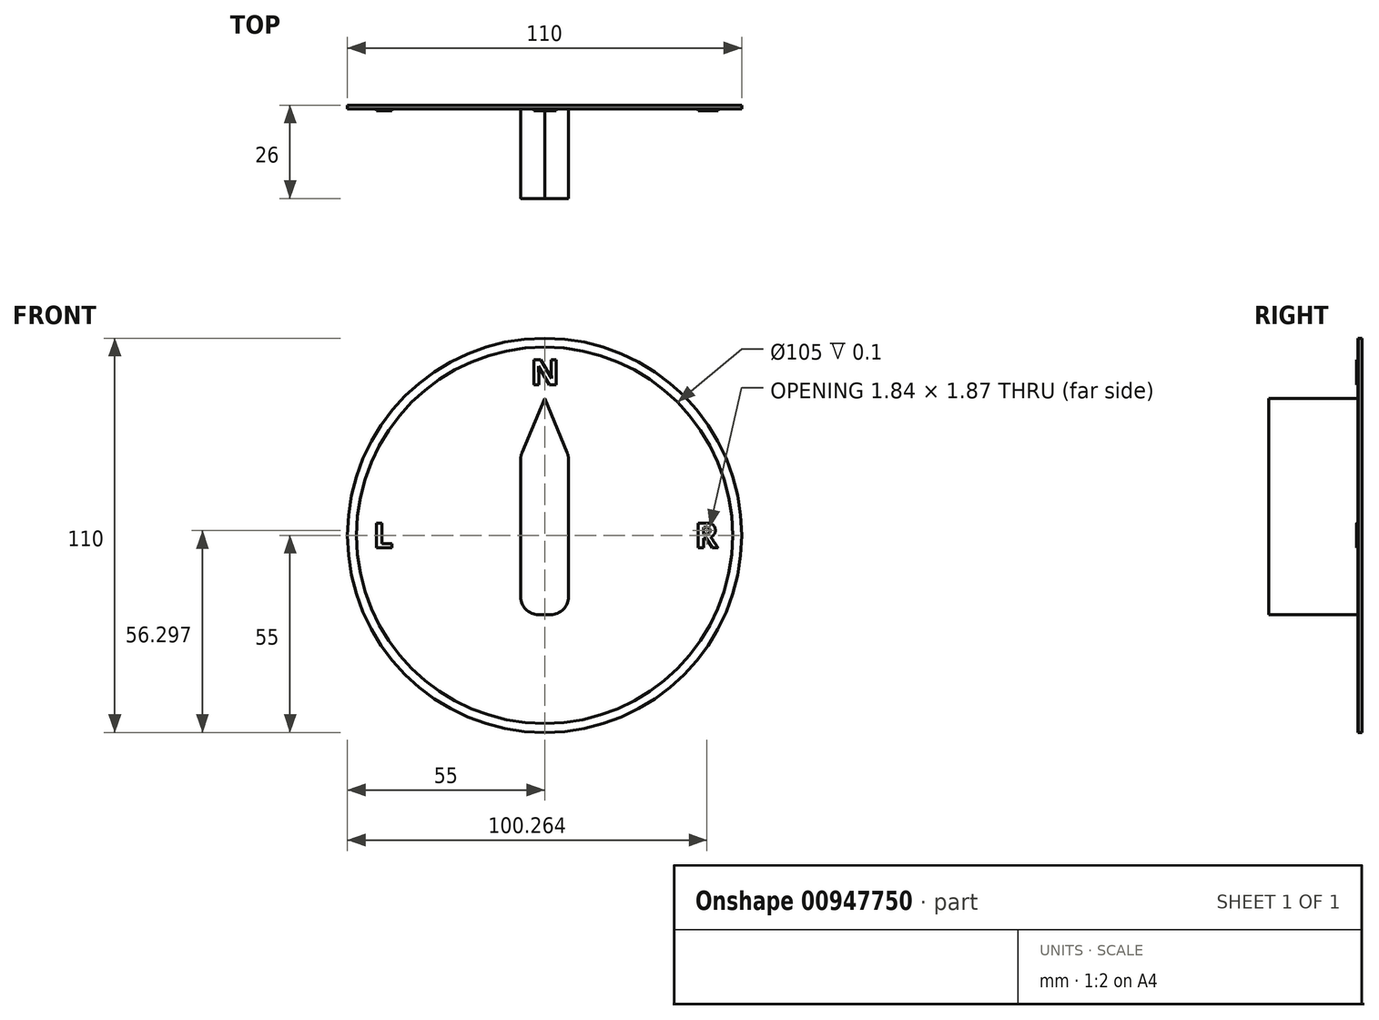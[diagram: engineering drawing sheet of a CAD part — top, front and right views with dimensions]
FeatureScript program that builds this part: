
annotation { "Feature Type Name" : "Feature", "Feature Type Description" : "" }
export const myFeature = defineFeature(function(context is Context, id is Id, definition is map)
    precondition{}
    {
        {
            var Q0;
            Q0=qCreatedBy(makeId("Right.planeOp"),FACE);
            var sketch = newSketch(context, id + "F0", { "sketchPlane" : qUnion([Q0])});
            skLineSegment(sketch, "E0", {"start": v(0, 0) * mm, "end": v(-116.06, 0) * mm, "construction": true});
            skSolve(sketch);
        }
        {
            var Q0;
            Q0=qCreatedBy(makeId("Right.planeOp"),FACE);
            var Q1;
            Q1=sQuery(id+"F0.wireOp",EDGE,"E0");
            cPlane(context, id + "F1", {"entities" : qUnion([Q0, Q1]), "cplaneType" : CPlaneType.LINE_ANGLE, "offset" : 25 * mm, "angle" : 2 * degree, "oppositeDirection" : true, "width" : 150 * mm, "height" : 150 * mm});
        }
        {
            var Q0;
            Q0=qCreatedBy(makeId("Front.planeOp"),FACE);
            var sketch = newSketch(context, id + "F2", { "sketchPlane" : qUnion([Q0])});
            skCircle(sketch, "E1", {"center": v(0, 0) * mm, "radius": 52.5 * mm});
            skCircle(sketch, "E2", {"center": v(0, 0) * mm, "radius": 55 * mm});
            skSolve(sketch);
        }
        {
            var Q0;
            Q0=qSketchRegion(id+"F2",true);
            extrude(context, id + "F3", {"entities" : qUnion([Q0]), "depth" : .1 * mm, "offsetDistance" : 25 * mm});
        }
        {
            var Q0;
            Q0=qCreatedBy(makeId("Front.planeOp"),FACE);
            var sketch = newSketch(context, id + "F4", { "sketchPlane" : qUnion([Q0])});
            skText(sketch, "E3", { "text": "N", "fontName": "OpenSans-Bold.ttf"});
            skLineSegment(sketch, "E4", {"start": v(0, 0) * mm, "end": v(0, 42) * mm, "construction": true});
            skLineSegment(sketch, "E5", {"start": v(0, 0) * mm, "end": v(42, 0) * mm, "construction": true});
            skLineSegment(sketch, "E6", {"start": v(0, 0) * mm, "end": v(-42, 0) * mm, "construction": true});
            skText(sketch, "E7", { "text": "L", "fontName": "OpenSans-Bold.ttf"});
            skPoint(sketch, "E8", {"position": v(-42, 0) * mm});
            skText(sketch, "E9", { "text": "R", "fontName": "OpenSans-Bold.ttf"});
            skPoint(sketch, "E10", {"position": v(42, 0) * mm});
            const initialGuessF4  = {"E3": [-0.00383, 0.042, 1, 0, 0.007], "E7": [-0.0478, -0.0035, 1, 0, 0.007], "E9": [0.042, -0.0035, 1, 0, 0.007]};
            skSetInitialGuess(sketch, initialGuessF4);
            skSolve(sketch);
        }
        {
            var Q0;
            Q0=qSketchRegion(id+"F4",true);
            extrude(context, id + "F5", {"entities" : qUnion([Q0]), "depth" : .5 * mm, "offsetDistance" : 25 * mm});
        }
        {
            var Q0;
            Q0=qCreatedBy(makeId("Front.planeOp"),FACE);
            var sketch = newSketch(context, id + "F6", { "sketchPlane" : qUnion([Q0])});
            skLineSegment(sketch, "E11.bottom", {"start": v(6.67, -22.16) * mm, "end": v(-6.67, -22.16) * mm});
            skLineSegment(sketch, "E11.left", {"start": v(6.67, -22.16) * mm, "end": v(6.67, 22.16) * mm});
            skLineSegment(sketch, "E11.right", {"start": v(-6.67, -22.16) * mm, "end": v(-6.67, 22.16) * mm});
            skPoint(sketch, "E11.middle", {"position": v(0, 0) * mm});
            skLineSegment(sketch, "E12", {"start": v(0, 38.16) * mm, "end": v(6.67, 22.16) * mm});
            skLineSegment(sketch, "E13", {"start": v(0, 38.16) * mm, "end": v(-6.67, 22.16) * mm});
            skSolve(sketch);
        }
        {
            var Q0;
            Q0=qSketchRegion(id+"F6",true);
            extrude(context, id + "F7", {"entities" : qUnion([Q0]), "depth" : 25 * mm, "offsetDistance" : 25 * mm});
        }
        {
            var Q0;
            Q0=makeQuery(id+"F7.opExtrude","SWEPT_EDGE",EDGE,{"disambiguationData":[OSD([sQuery(id+"F6.wireOp",EDGE,"E11.right"),sQuery(id+"F6.wireOp",EDGE,"E13")])]});
            var Q1;
            Q1=makeQuery(id+"F7.opExtrude","SWEPT_EDGE",EDGE,{"disambiguationData":[OSD([sQuery(id+"F6.wireOp",EDGE,"E11.left"),sQuery(id+"F6.wireOp",EDGE,"E12")])]});
            var Q2;
            Q2=makeQuery(id+"F7.opExtrude","SWEPT_EDGE",EDGE,{"disambiguationData":[OSD([sQuery(id+"F6.wireOp",EDGE,"E11.bottom"),sQuery(id+"F6.wireOp",EDGE,"E11.left")])]});
            var Q3;
            Q3=makeQuery(id+"F7.opExtrude","SWEPT_EDGE",EDGE,{"disambiguationData":[OSD([sQuery(id+"F6.wireOp",EDGE,"E11.bottom"),sQuery(id+"F6.wireOp",EDGE,"E11.right")])]});
            fillet(context, id + "F8", {"entities" : qUnion([Q0, Q1, Q2, Q3]), "radius" : 5 * mm, "tangentPropagation" : true, "allowEdgeOverflow" : false});
        }
        {
            var Q0;
            Q0=qCreatedBy(makeId("Front.planeOp"),FACE);
            var sketch = newSketch(context, id + "F9", { "sketchPlane" : qUnion([Q0])});
            skCircle(sketch, "E14", {"center": v(0, 0) * mm, "radius": 55 * mm});
            skSolve(sketch);
        }
        {
            var Q0;
            Q0=qSketchRegion(id+"F9",true);
            extrude(context, id + "F10", {"entities" : qUnion([Q0]), "oppositeDirection" : true, "depth" : 1 * mm, "offsetDistance" : 25 * mm});
        }
    });
